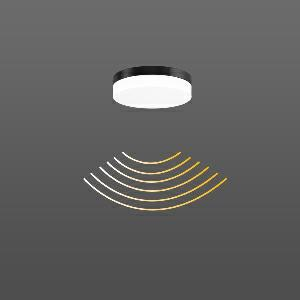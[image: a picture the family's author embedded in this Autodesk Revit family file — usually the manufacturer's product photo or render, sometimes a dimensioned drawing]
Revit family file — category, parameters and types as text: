
# Revit family: flat_slim_round_312135_0031_19_5d3a
name_source: partatom
category: Lighting Fixtures
units: mm (PartAtom-declared; Revit-internal decimal feet)

## family parameters
Cut with Voids When Loaded = No
Host = Face
Light Source = No
Part Type = Normal
Room Calculation Point = No
Round Connector Dimension = Use Diameter
Shared = No

## types (1)
- FLAT SLIM round (1 x LED Modul 830, 1150 lm, 3000)
    Apparent Load = 12 VA
    CIE Flux Codes = 43 74 92 91 100
    Color Rendering = 80
    Color Temperature = 3000
    Default Elevation = 1800 mm
    Height = 63 mm
    Lamp = 1 x LED Modul 830
    Lamp Light Flux = 1150 lm
    Lamp count = 1
    Length = 230 mm
    Lifetime = 50000 h
    Luminous efficacy = 96 lm/W
    Manufacturer = RZB
    ModVariant = No
    Model = 312135.0031.19
    Mounting Place = Ceiling, Wall
    Mounting Type = Surface mounted
    Number of Poles = 1
    OnlyDefault = Yes
    Power Factor = 1
    Product Name = FLAT SLIM round
    Product group = Surface mounted ceiling and wall luminaires
    ProductGroupID = 305
    Protection Class = Protection class I
    Protection Degree = IP 65
    RLX_Detail_Level = 1
    RLX_Emergency_Light_Flux = 0 lm
    RLX_Emergency_Type = 0
    RLX_Emergency_Type_DB = No
    RlxData = <blob elided: 31885 chars, md5=a86f6f07>
    Socket = socket
    Standby Power = 0 W
    System Light Flux = 1150 lm
    System Power = 12 W
    Type Comments = Product without accessories
    Type Image = 312132.0031.19.jpg
    URL = http://relux.com
    VarID = ---
    Voltage = 230 V
    Voltage Range = 220-240 V
    Weight = 0.00 kg
    Width = 0 mm  [stored 0 ft]

note: [stored X ft] marks values corroborated as IEEE doubles in the binary element streams (Revit-internal decimal feet)

## geometry (parser evidence)
native form markers: Blend x4, Sweep x10
no freeform markers — native parametric forms only
